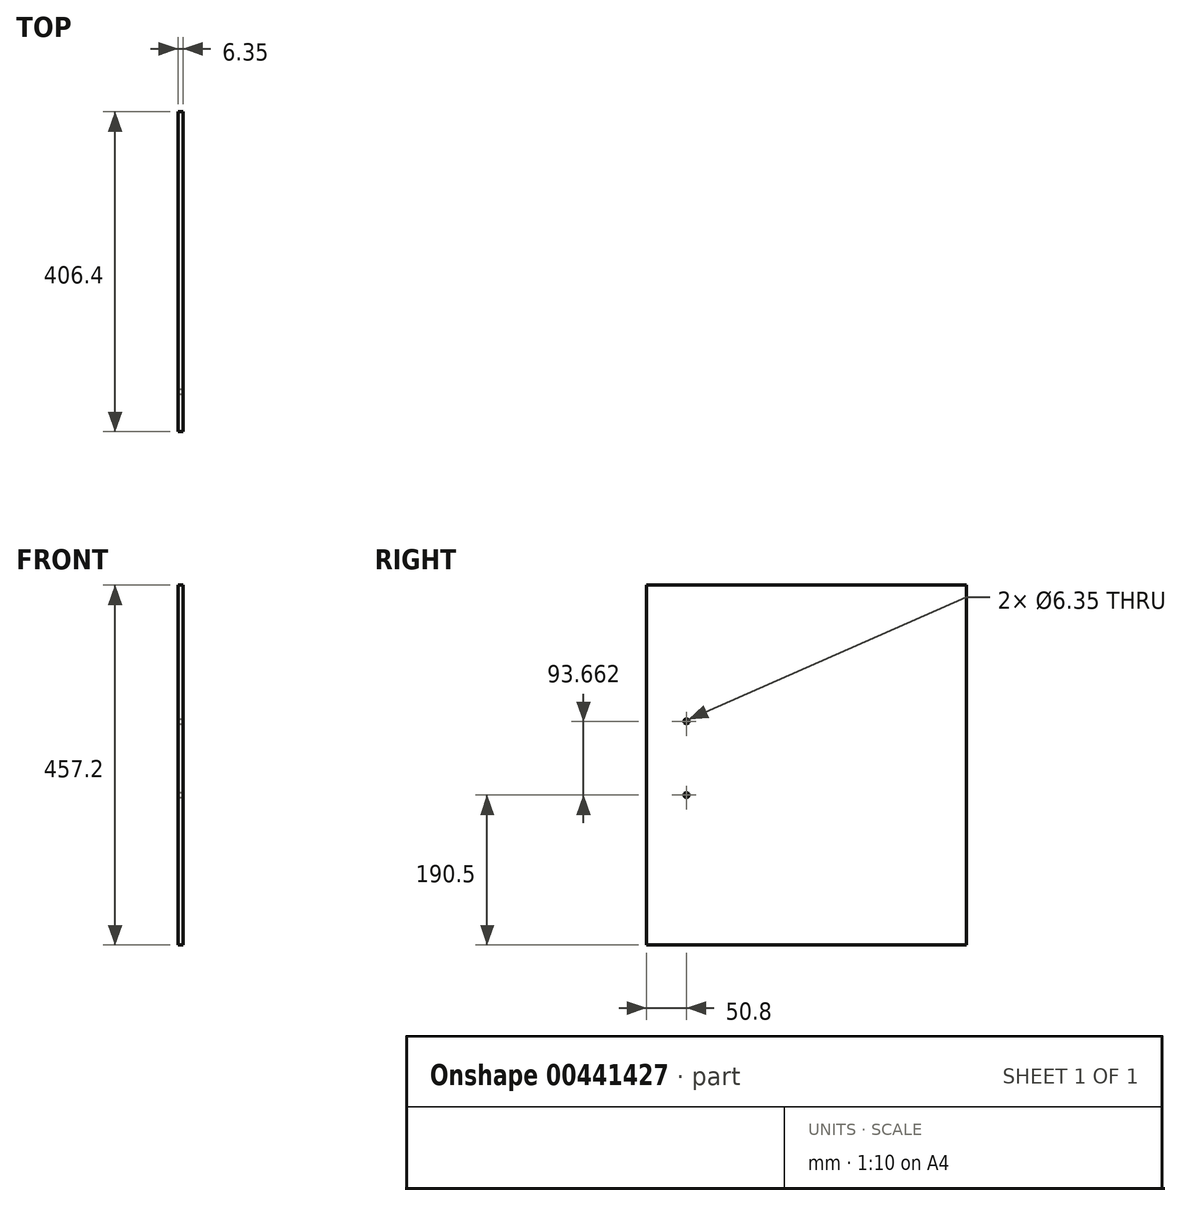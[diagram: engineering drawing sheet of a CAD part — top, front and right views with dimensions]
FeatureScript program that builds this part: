
annotation { "Feature Type Name" : "Feature", "Feature Type Description" : "" }
export const myFeature = defineFeature(function(context is Context, id is Id, definition is map)
    precondition{}
    {
        {
            var Q0;
            Q0=qCreatedBy(makeId("Right.planeOp"),FACE);
            var sketch = newSketch(context, id + "F0", { "sketchPlane" : qUnion([Q0])});
            skLineSegment(sketch, "E0.bottom", {"start": v(-203.2, 228.6) * mm, "end": v(203.2, 228.6) * mm});
            skLineSegment(sketch, "E0.top", {"start": v(-203.2, -228.6) * mm, "end": v(203.2, -228.6) * mm});
            skLineSegment(sketch, "E0.left", {"start": v(-203.2, 228.6) * mm, "end": v(-203.2, -228.6) * mm});
            skLineSegment(sketch, "E0.right", {"start": v(203.2, 228.6) * mm, "end": v(203.2, -228.6) * mm});
            skPoint(sketch, "E0.middle", {"position": v(0, 0) * mm});
            skSolve(sketch);
        }
        {
            var Q0;
            Q0 = qSketchRegion(id + "F0", true);
            extrude(context, id + "F1", {"entities" : qUnion([Q0]), "depth" : 6.35 * mm});
        }
        {
            var Q0;
            Q0=makeQuery(id+"F1.opExtrude","CAP_FACE",FACE,{"disambiguationData":[OSD([sQuery(id+"F0.wireOp",EDGE,"E0.bottom"),sQuery(id+"F0.wireOp",EDGE,"E0.top"),sQuery(id+"F0.wireOp",EDGE,"E0.left"),sQuery(id+"F0.wireOp",EDGE,"E0.right")])],"isStart":false});
            var sketch = newSketch(context, id + "F2", { "sketchPlane" : qUnion([Q0])});
            skCircle(sketch, "E1", {"center": v(-152.4, -38.1) * mm, "radius": 3.18 * mm});
            skCircle(sketch, "E2", {"center": v(-152.4, 55.56) * mm, "radius": 3.18 * mm});
            skSolve(sketch);
        }
        {
            var Q0;
            Q0 = qSketchRegion(id + "F2", true);
            extrude(context, id + "F3", {"entities" : qUnion([Q0]), "operationType" : NewBodyOperationType.REMOVE, "endBound" : BoundingType.THROUGH_ALL, "oppositeDirection" : true, "depth" : 25.4 * mm});
        }
    });
